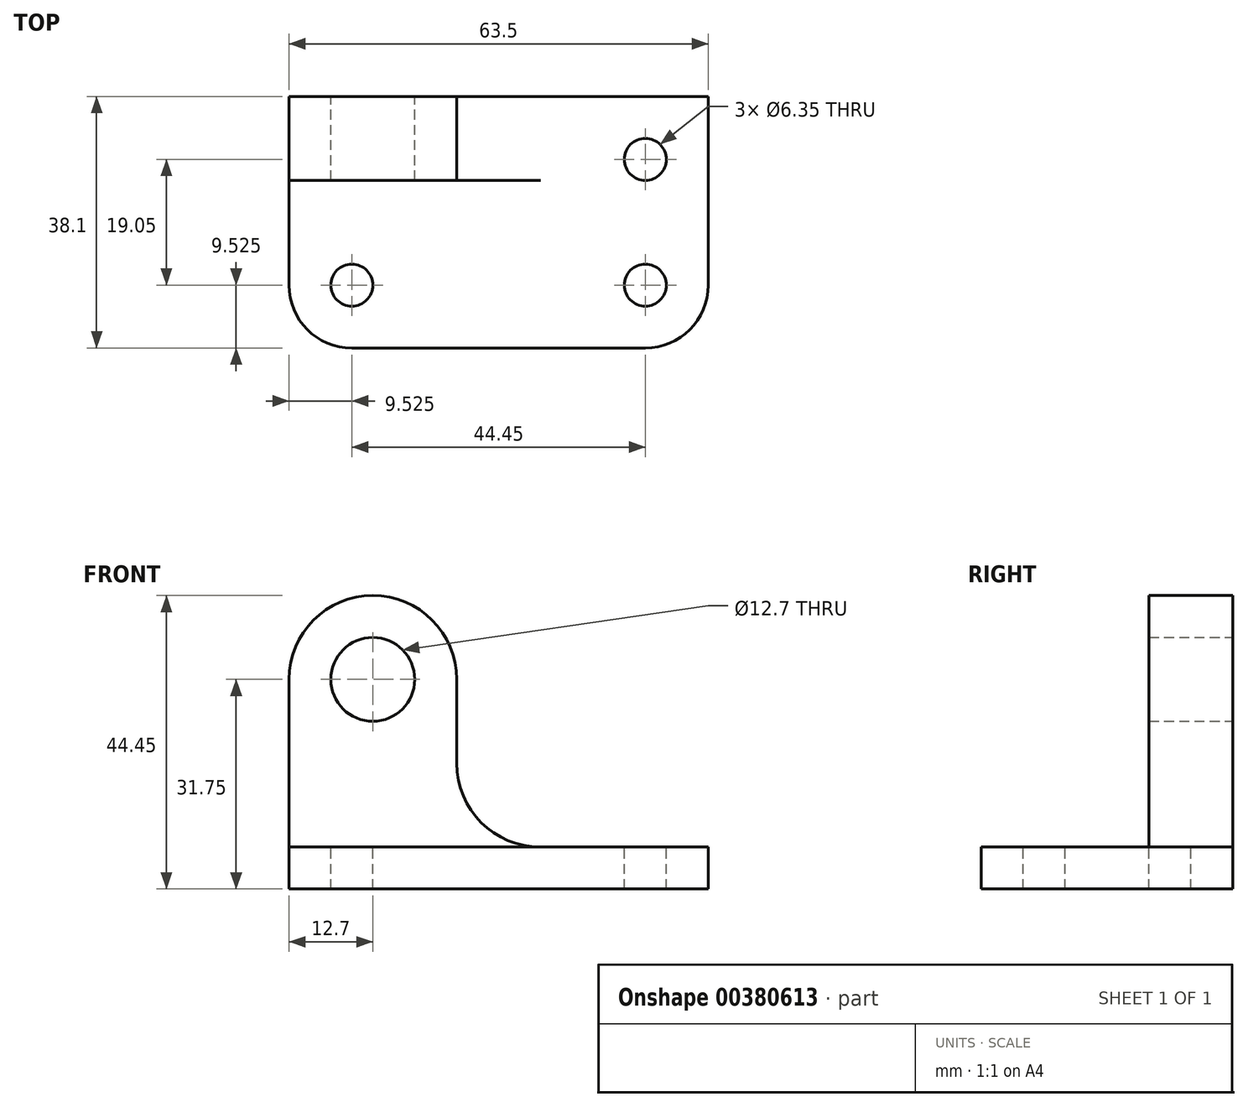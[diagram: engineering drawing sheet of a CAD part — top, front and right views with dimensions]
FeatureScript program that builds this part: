
annotation { "Feature Type Name" : "Feature", "Feature Type Description" : "" }
export const myFeature = defineFeature(function(context is Context, id is Id, definition is map)
    precondition{}
    {
        {
            var Q0;
            Q0=qCreatedBy(makeId("Right.planeOp"),FACE);
            var sketch = newSketch(context, id + "F0", { "sketchPlane" : qUnion([Q0])});
            skLineSegment(sketch, "E0", {"start": v(0, 0) * mm, "end": v(38.1, 0) * mm});
            skLineSegment(sketch, "E1", {"start": v(38.1, 0) * mm, "end": v(38.1, 44.45) * mm});
            skLineSegment(sketch, "E2", {"start": v(38.1, 44.45) * mm, "end": v(0, 44.45) * mm});
            skLineSegment(sketch, "E3", {"start": v(0, 44.45) * mm, "end": v(0, 0) * mm});
            skSolve(sketch);
        }
        {
            var Q0;
            Q0 = qSketchRegion(id + "F0", true);
            extrude(context, id + "F1", {"entities" : qUnion([Q0]), "depth" : 63.5 * mm});
        }
        {
            var Q0;
            Q0=makeQuery(id+"F1.opExtrude","SWEPT_FACE",FACE,{"disambiguationData":[OSD([sQuery(id+"F0.wireOp",EDGE,"E1")])]});
            var sketch = newSketch(context, id + "F2", { "sketchPlane" : qUnion([Q0])});
            skLineSegment(sketch, "E4", {"start": v(0, 6.35) * mm, "end": v(-25.4, 6.35) * mm});
            skArc(sketch, "E5", {"start": v(-38.1, 31.75) * mm, "mid": v(-50.8, 44.45) * mm, "end": v(-63.5, 31.75) * mm});
            skArc(sketch, "E6", {"start": v(-38.1, 19.05) * mm, "mid": v(-34.38, 10.07) * mm, "end": v(-25.4, 6.35) * mm});
            skLineSegment(sketch, "E7", {"start": v(-38.1, 31.75) * mm, "end": v(-38.1, 19.05) * mm});
            skCircle(sketch, "E8", {"center": v(-50.8, 31.75) * mm, "radius": 6.35 * mm});
            skSolve(sketch);
        }
        {
            var Q0;
            Q0 = qSketchRegion(id + "F2", true);
            var Q1;
            {var subQ5=sQuery(id+"F2.wireOp",EDGE,"E4");Q1=makeQuery(id+"F2.imprint","IMPRINT",FACE,{"disambiguationData":[TD([[makeQuery(id+"F2.imprint","IMPRINT",EDGE,{"derivedFrom":subQ5}),-1.0]])]});}
            var Q2;
            {var subQ0=sQuery(id+"F2.wireOp",EDGE,"E5");var subQ1=sQuery(id+"F0.wireOp",EDGE,"E1");var subQ2=makeQuery(id+"F1.opExtrude","CAP_EDGE",EDGE,{"disambiguationData":[OSD([subQ1])],"isStart":false});var subQ3=makeQuery(id+"F2.imprint","INTERSECT",VERTEX,{"derivedFrom":[subQ2,subQ0]});Q2=makeQuery(id+"F2.imprint","IMPRINT",FACE,{"disambiguationData":[TD([[makeQuery(id+"F2.imprint","IMPRINT",EDGE,{"disambiguationData":[TD([[subQ3,1.0]])],"derivedFrom":subQ0}),-1.0]])]});}
            extrude(context, id + "F3", {"entities" : qUnion([Q0, Q1, Q2]), "operationType" : NewBodyOperationType.REMOVE, "oppositeDirection" : true, "depth" : 76.2 * mm});
        }
        {
            var Q0;
            Q0=makeQuery(id+"F1.opExtrude","CAP_FACE",FACE,{"disambiguationData":[OSD([sQuery(id+"F0.wireOp",EDGE,"E0"),sQuery(id+"F0.wireOp",EDGE,"E1"),sQuery(id+"F0.wireOp",EDGE,"E2"),sQuery(id+"F0.wireOp",EDGE,"E3")])],"isStart":false});
            var sketch = newSketch(context, id + "F4", { "sketchPlane" : qUnion([Q0])});
            skLineSegment(sketch, "E9", {"start": v(25.4, 31.75) * mm, "end": v(25.4, 6.35) * mm});
            skLineSegment(sketch, "E10", {"start": v(25.4, 6.35) * mm, "end": v(0, 6.35) * mm});
            skSolve(sketch);
        }
        {
            var Q0;
            {var subQ0=sQuery(id+"F4.wireOp",EDGE,"E9");Q0=makeQuery(id+"F4.imprint","IMPRINT",FACE,{"disambiguationData":[TD([[makeQuery(id+"F4.imprint","IMPRINT",EDGE,{"derivedFrom":subQ0}),-1.0]])]});}
            extrude(context, id + "F5", {"entities" : qUnion([Q0]), "operationType" : NewBodyOperationType.REMOVE, "oppositeDirection" : true, "depth" : 76.2 * mm});
        }
        {
            var Q0;
            Q0=makeQuery(id+"F5.boolean.opBoolean","MERGE",FACE,{"derivedFrom":[makeQuery(id+"F3.boolean.opBoolean","COPY",FACE,{"derivedFrom":makeQuery(id+"F3.opExtrude","SWEPT_FACE",FACE,{"disambiguationData":[OSD([sQuery(id+"F2.wireOp",EDGE,"E4")])]})}),makeQuery(id+"F5.opExtrude","SWEPT_FACE",FACE,{"disambiguationData":[OSD([sQuery(id+"F4.wireOp",EDGE,"E10")])]})]});
            extrude(context, id + "F6", {"entities" : qUnion([Q0]), "operationType" : NewBodyOperationType.ADD, "depth" : 50.8 * mm});
        }
        {
            var Q0;
            {var subQ0=sQuery(id+"F0.wireOp",EDGE,"E1");Q0=makeQuery(id+"F6.boolean.opBoolean","MERGE",FACE,{"derivedFrom":[makeQuery(id+"F1.opExtrude","CAP_FACE",FACE,{"disambiguationData":[OSD([sQuery(id+"F0.wireOp",EDGE,"E0"),subQ0,sQuery(id+"F0.wireOp",EDGE,"E2"),sQuery(id+"F0.wireOp",EDGE,"E3")])],"isStart":true}),makeQuery(id+"F6.opExtrude","SWEPT_FACE",FACE,{"disambiguationData":[OSD([subQ0,sQuery(id+"F2.wireOp",EDGE,"E4")])]})]});}
            var sketch = newSketch(context, id + "F7", { "sketchPlane" : qUnion([Q0])});
            skLineSegment(sketch, "E11", {"start": v(-38.1, 6.35) * mm, "end": v(0, 6.35) * mm});
            skSolve(sketch);
        }
        {
            var Q0;
            {var subQ0=sQuery(id+"F7.wireOp",EDGE,"E11");Q0=makeQuery(id+"F7.imprint","IMPRINT",FACE,{"disambiguationData":[TD([[makeQuery(id+"F7.imprint","IMPRINT",EDGE,{"derivedFrom":subQ0}),1.0]])]});}
            extrude(context, id + "F8", {"entities" : qUnion([Q0]), "operationType" : NewBodyOperationType.REMOVE, "oppositeDirection" : true, "depth" : 25.4 * mm});
        }
        {
            var Q0;
            Q0=makeQuery(id+"F6.boolean.opBoolean","MERGE",FACE,{"derivedFrom":[makeQuery(id+"F1.opExtrude","CAP_FACE",FACE,{"disambiguationData":[OSD([sQuery(id+"F0.wireOp",EDGE,"E0"),sQuery(id+"F0.wireOp",EDGE,"E1"),sQuery(id+"F0.wireOp",EDGE,"E2"),sQuery(id+"F0.wireOp",EDGE,"E3")])],"isStart":false}),makeQuery(id+"F6.opExtrude","SWEPT_FACE",FACE,{"disambiguationData":[OSD([sQuery(id+"F4.wireOp",EDGE,"E10")])]})]});
            var sketch = newSketch(context, id + "F9", { "sketchPlane" : qUnion([Q0])});
            skLineSegment(sketch, "E12", {"start": v(25.4, 31.75) * mm, "end": v(25.4, 6.35) * mm});
            skLineSegment(sketch, "E13", {"start": v(25.4, 6.35) * mm, "end": v(0, 6.35) * mm});
            skSolve(sketch);
        }
        {
            var Q0;
            Q0=makeQuery(id+"F9.imprint","IMPRINT",FACE,{"disambiguationData":[TD([[makeQuery(id+"F9.imprint","IMPRINT",EDGE,{"derivedFrom":sQuery(id+"F9.wireOp",EDGE,"E12")}),-1.0]])]});
            extrude(context, id + "F10", {"entities" : qUnion([Q0]), "operationType" : NewBodyOperationType.REMOVE, "oppositeDirection" : true, "depth" : 76.2 * mm, "hasDraft" : true, "draftAngle" : 0 * degree});
        }
        {
            var Q0;
            Q0=makeQuery(id+"F10.boolean.opBoolean","MERGE",FACE,{"derivedFrom":[makeQuery(id+"F8.boolean.opBoolean","COPY",FACE,{"derivedFrom":makeQuery(id+"F8.opExtrude","SWEPT_FACE",FACE,{"disambiguationData":[OSD([sQuery(id+"F7.wireOp",EDGE,"E11")])]})}),makeQuery(id+"F10.opExtrude","SWEPT_FACE",FACE,{"disambiguationData":[OSD([sQuery(id+"F9.wireOp",EDGE,"E13")])]})]});
            var sketch = newSketch(context, id + "F11", { "sketchPlane" : qUnion([Q0])});
            skArc(sketch, "E14", {"start": v(0, 9.52) * mm, "mid": v(2.79, 2.79) * mm, "end": v(9.53, 0) * mm});
            skCircle(sketch, "E15", {"center": v(9.53, 9.52) * mm, "radius": 3.18 * mm});
            skCircle(sketch, "E16", {"center": v(53.98, 9.53) * mm, "radius": 3.18 * mm});
            skCircle(sketch, "E17", {"center": v(9.52, 28.58) * mm, "radius": 3.18 * mm});
            skArc(sketch, "E18", {"start": v(53.98, 0) * mm, "mid": v(60.71, 2.79) * mm, "end": v(63.5, 9.53) * mm});
            skSolve(sketch);
        }
        {
            var Q0;
            {var subQ0=sQuery(id+"F11.wireOp",EDGE,"E14");Q0=makeQuery(id+"F11.imprint","IMPRINT",FACE,{"disambiguationData":[TD([[makeQuery(id+"F11.imprint","IMPRINT",EDGE,{"derivedFrom":subQ0}),-1.0]])]});}
            var Q1;
            Q1=makeQuery(id+"F11.imprint","IMPRINT",FACE,{"disambiguationData":[TD([[makeQuery(id+"F11.imprint","IMPRINT",EDGE,{"derivedFrom":sQuery(id+"F11.wireOp",EDGE,"E15")}),1.0]])]});
            var Q2;
            Q2=makeQuery(id+"F11.imprint","IMPRINT",FACE,{"disambiguationData":[TD([[makeQuery(id+"F11.imprint","IMPRINT",EDGE,{"derivedFrom":sQuery(id+"F11.wireOp",EDGE,"E16")}),1.0]])]});
            var Q3;
            {var subQ0=sQuery(id+"F11.wireOp",EDGE,"KBLp3CoG-kTUa-TUTr-mOAm-0BXdPAIyydLt");Q3=makeQuery(id+"F11.imprint","IMPRINT",FACE,{"disambiguationData":[TD([[makeQuery(id+"F11.imprint","IMPRINT",EDGE,{"derivedFrom":subQ0}),-1.0]])]});}
            var Q4;
            Q4=makeQuery(id+"F11.imprint","IMPRINT",FACE,{"disambiguationData":[TD([[makeQuery(id+"F11.imprint","IMPRINT",EDGE,{"derivedFrom":sQuery(id+"F11.wireOp",EDGE,"E17")}),1.0]])]});
            var Q5;
            {var subQ0=sQuery(id+"F11.wireOp",EDGE,"E18");Q5=makeQuery(id+"F11.imprint","IMPRINT",FACE,{"disambiguationData":[TD([[makeQuery(id+"F11.imprint","IMPRINT",EDGE,{"derivedFrom":subQ0}),-1.0]])]});}
            extrude(context, id + "F12", {"entities" : qUnion([Q0, Q1, Q2, Q3, Q4, Q5]), "operationType" : NewBodyOperationType.REMOVE, "oppositeDirection" : true, "depth" : 25.4 * mm});
        }
        {
            var Q0;
            Q0=makeQuery(id+"F1.opExtrude","SWEPT_BODY",BODY,{"disambiguationData":[OSD([sQuery(id+"F0.wireOp",EDGE,"E0"),sQuery(id+"F0.wireOp",EDGE,"E1"),sQuery(id+"F0.wireOp",EDGE,"E2"),sQuery(id+"F0.wireOp",EDGE,"E3")])]});
            var Q1;
            Q1=qCreatedBy(makeId("Right.planeOp"),FACE);
            mirror(context, id + "F13", {"entities" : qUnion([Q0]), "mirrorPlane" : qUnion([Q1])});
        }
        {
            var Q0;
            Q0=makeQuery(id+"F13.opPattern","COPY",BODY,{"derivedFrom":makeQuery(id+"F1.opExtrude","SWEPT_BODY",BODY,{"disambiguationData":[OSD([sQuery(id+"F0.wireOp",EDGE,"E0"),sQuery(id+"F0.wireOp",EDGE,"E1"),sQuery(id+"F0.wireOp",EDGE,"E2"),sQuery(id+"F0.wireOp",EDGE,"E3")])]}),"instanceName":"1"});
            var Q1;
            Q1=qCreatedBy(makeId("Right.planeOp"),FACE);
            mirror(context, id + "F14", {"operationType" : NewBodyOperationType.REMOVE, "entities" : qUnion([Q0]), "mirrorPlane" : qUnion([Q1])});
        }
    });
